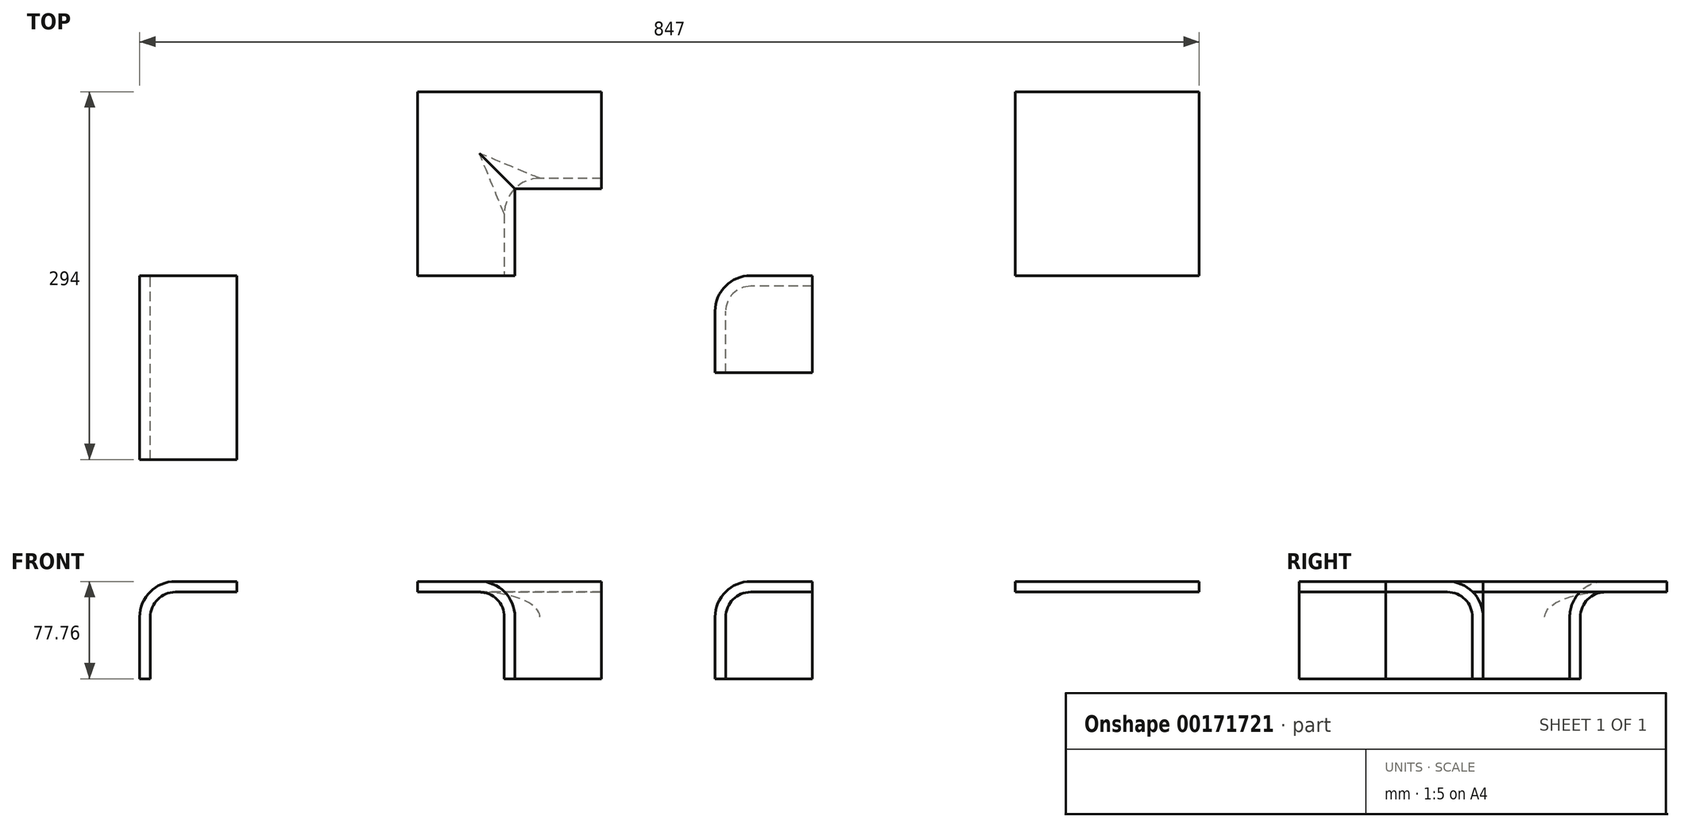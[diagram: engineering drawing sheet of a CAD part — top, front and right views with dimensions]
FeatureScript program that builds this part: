
annotation { "Feature Type Name" : "Feature", "Feature Type Description" : "" }
export const myFeature = defineFeature(function(context is Context, id is Id, definition is map)
    precondition{}
    {
        {
            var Q0;
            Q0=qCreatedBy(makeId("Front.planeOp"),FACE);
            var sketch = newSketch(context, id + "F0", { "sketchPlane" : qUnion([Q0])});
            skLineSegment(sketch, "E0.bottom", {"start": v(-500, 38.88) * mm, "end": v(500, 38.88) * mm, "construction": true});
            skLineSegment(sketch, "E0.top", {"start": v(-500, -38.87) * mm, "end": v(500, -38.87) * mm, "construction": true});
            skLineSegment(sketch, "E0.left", {"start": v(-500, 38.88) * mm, "end": v(-500, -38.87) * mm, "construction": true});
            skLineSegment(sketch, "E0.right", {"start": v(500, 38.87) * mm, "end": v(500, -38.88) * mm, "construction": true});
            skPoint(sketch, "E0.middle", {"position": v(0, 0) * mm});
            skLineSegment(sketch, "E1", {"start": v(-500, -38.87) * mm, "end": v(-500, 38.88) * mm});
            skLineSegment(sketch, "E2", {"start": v(-500, 38.88) * mm, "end": v(-422.25, 38.88) * mm});
            skLineSegment(sketch, "E3", {"start": v(-422.25, 38.88) * mm, "end": v(-422.25, 30.38) * mm});
            skLineSegment(sketch, "E4", {"start": v(-422.25, 30.38) * mm, "end": v(-491.5, 30.38) * mm});
            skLineSegment(sketch, "E5", {"start": v(-491.5, 30.38) * mm, "end": v(-491.5, -38.87) * mm});
            skLineSegment(sketch, "E6", {"start": v(-491.5, -38.87) * mm, "end": v(-500, -38.87) * mm});
            skLineSegment(sketch, "E7", {"start": v(-350, 38.88) * mm, "end": v(-350, -45.08) * mm, "construction": true});
            skLineSegment(sketch, "E8.MirrorCS", {"start": v(-208.5, -38.87) * mm, "end": v(-200, -38.87) * mm});
            skLineSegment(sketch, "E9.MirrorCS", {"start": v(-277.75, 38.88) * mm, "end": v(-277.75, 30.38) * mm});
            skLineSegment(sketch, "E10.MirrorCS", {"start": v(-200, 38.88) * mm, "end": v(-200, -38.87) * mm, "construction": true});
            skLineSegment(sketch, "E11.MirrorCS", {"start": v(-200, 38.88) * mm, "end": v(-1200, 38.88) * mm, "construction": true});
            skLineSegment(sketch, "E12.MirrorCS", {"start": v(-200, -38.87) * mm, "end": v(-1200, -38.87) * mm, "construction": true});
            skLineSegment(sketch, "E13.MirrorCS", {"start": v(-200, -38.87) * mm, "end": v(-200, 38.88) * mm});
            skLineSegment(sketch, "E14.MirrorCS", {"start": v(-277.75, 30.38) * mm, "end": v(-208.5, 30.38) * mm});
            skLineSegment(sketch, "E15.MirrorCS", {"start": v(-208.5, 30.38) * mm, "end": v(-208.5, -38.87) * mm});
            skLineSegment(sketch, "E16.MirrorCS", {"start": v(-200, 38.88) * mm, "end": v(-277.75, 38.88) * mm});
            skLineSegment(sketch, "E17", {"start": v(-120, 38.88) * mm, "end": v(-120, -38.87) * mm, "construction": true});
            skLineSegment(sketch, "E18.MirrorCS", {"start": v(-31.5, -38.87) * mm, "end": v(-40, -38.87) * mm});
            skLineSegment(sketch, "E19.MirrorCS", {"start": v(37.75, 38.88) * mm, "end": v(37.75, 30.38) * mm});
            skLineSegment(sketch, "E20.MirrorCS", {"start": v(-40, 38.88) * mm, "end": v(-40, -38.87) * mm, "construction": true});
            skLineSegment(sketch, "E21.MirrorCS", {"start": v(-40, -38.87) * mm, "end": v(-40, 38.88) * mm});
            skLineSegment(sketch, "E22.MirrorCS", {"start": v(-31.5, 30.38) * mm, "end": v(-31.5, -38.87) * mm});
            skLineSegment(sketch, "E23.MirrorCS", {"start": v(37.75, 30.38) * mm, "end": v(-31.5, 30.38) * mm});
            skLineSegment(sketch, "E24.MirrorCS", {"start": v(-40, 38.88) * mm, "end": v(37.75, 38.88) * mm});
            skPoint(sketch, "E25.oppositeSnap0", {"position": v(500, 0) * mm});
            skLineSegment(sketch, "E25.bottom", {"start": v(200, 38.88) * mm, "end": v(347, 38.88) * mm});
            skLineSegment(sketch, "E25.top", {"start": v(200, 30.38) * mm, "end": v(347, 30.38) * mm});
            skLineSegment(sketch, "E25.left", {"start": v(200, 38.88) * mm, "end": v(200, 30.38) * mm});
            skLineSegment(sketch, "E25.right", {"start": v(347, 38.88) * mm, "end": v(347, 30.38) * mm});
            skSolve(sketch);
        }
        {
            var Q0;
            Q0=makeQuery(id+"F0.imprint","IMPRINT",FACE,{"disambiguationData":[TD([[makeQuery(id+"F0.imprint","IMPRINT",EDGE,{"derivedFrom":sQuery(id+"F0.wireOp",EDGE,"E1")}),-1.0]])]});
            extrude(context, id + "F1", {"entities" : qUnion([Q0]), "depth" : 147 * mm});
        }
        {
            var Q0;
            Q0=makeQuery(id+"F0.imprint","IMPRINT",FACE,{"disambiguationData":[TD([[makeQuery(id+"F0.imprint","IMPRINT",EDGE,{"derivedFrom":sQuery(id+"F0.wireOp",EDGE,"E8.MirrorCS")}),1.0]])]});
            extrude(context, id + "F2", {"entities" : qUnion([Q0]), "oppositeDirection" : true, "depth" : 147 * mm});
        }
        {
            var Q0;
            Q0=makeQuery(id+"F0.imprint","IMPRINT",FACE,{"disambiguationData":[TD([[makeQuery(id+"F0.imprint","IMPRINT",EDGE,{"derivedFrom":sQuery(id+"F0.wireOp",EDGE,"E18.MirrorCS")}),-1.0]])]});
            extrude(context, id + "F3", {"entities" : qUnion([Q0]), "depth" : 77.75 * mm});
        }
        {
            var Q0;
            Q0=makeQuery(id+"F2.opExtrude","SWEPT_FACE",FACE,{"disambiguationData":[OSD([sQuery(id+"F0.wireOp",EDGE,"E13.MirrorCS")])]});
            var sketch = newSketch(context, id + "F4", { "sketchPlane" : qUnion([Q0])});
            skLineSegment(sketch, "E26.0.1", {"start": v(69.25, -38.87) * mm, "end": v(77.75, -38.87) * mm});
            skLineSegment(sketch, "E26.0.2", {"start": v(147, 30.38) * mm, "end": v(147, 38.88) * mm});
            skLineSegment(sketch, "E26.0.3", {"start": v(147, 38.88) * mm, "end": v(69.25, 38.88) * mm});
            skLineSegment(sketch, "E27", {"start": v(69.25, 38.88) * mm, "end": v(69.25, -38.87) * mm});
            skLineSegment(sketch, "E28", {"start": v(77.75, -38.87) * mm, "end": v(77.75, 30.38) * mm});
            skLineSegment(sketch, "E29", {"start": v(77.75, 30.38) * mm, "end": v(147, 30.38) * mm});
            skPoint(sketch, "E30.orphan", {"position": v(147, -38.87) * mm});
            skPoint(sketch, "E26.0.0.end.orphan", {"position": v(0, -38.87) * mm});
            skPoint(sketch, "E26.0.0.start.orphan", {"position": v(0, 38.88) * mm});
            skLineSegment(sketch, "E31", {"start": v(77.75, -38.87) * mm, "end": v(69.25, -38.87) * mm});
            skSolve(sketch);
        }
        {
            var Q0;
            Q0=makeQuery(id+"F4.imprint","IMPRINT",FACE,{"disambiguationData":[TD([[makeQuery(id+"F4.imprint","IMPRINT",EDGE,{"derivedFrom":sQuery(id+"F4.wireOp",EDGE,"E26.0.3")}),1.0]])]});
            extrude(context, id + "F5", {"entities" : qUnion([Q0]), "operationType" : NewBodyOperationType.ADD, "depth" : 69.25 * mm});
        }
        {
            var Q0;
            {var subQ0=sQuery(id+"F0.wireOp",EDGE,"E13.MirrorCS");Q0=makeQuery(id+"F5.boolean.opBoolean","SPLIT",FACE,{"disambiguationData":[TD([makeQuery(id+"F5.opExtrude","SWEPT_FACE",FACE,{"disambiguationData":[OSD([sQuery(id+"F4.wireOp",EDGE,"E28")])]})])],"derivedFrom":makeQuery(id+"F2.opExtrude","SWEPT_FACE",FACE,{"disambiguationData":[OSD([subQ0])]})});}
            extrude(context, id + "F6", {"entities" : qUnion([Q0]), "operationType" : NewBodyOperationType.REMOVE, "oppositeDirection" : true, "depth" : 25 * mm});
        }
        {
            var Q0;
            Q0=makeQuery(id+"F0.imprint","IMPRINT",FACE,{"disambiguationData":[TD([[makeQuery(id+"F0.imprint","IMPRINT",EDGE,{"derivedFrom":sQuery(id+"F0.wireOp",EDGE,"E18.MirrorCS")}),-1.0]])]});
            var sketch = newSketch(context, id + "F7", { "sketchPlane" : qUnion([Q0])});
            skLineSegment(sketch, "E32.0", {"start": v(-40, 38.88) * mm, "end": v(37.75, 38.88) * mm});
            skLineSegment(sketch, "E33.0", {"start": v(-40, -38.87) * mm, "end": v(-40, 38.88) * mm});
            skLineSegment(sketch, "E34", {"start": v(37.75, 38.88) * mm, "end": v(37.75, -38.87) * mm});
            skLineSegment(sketch, "E35", {"start": v(37.75, -38.87) * mm, "end": v(-40, -38.87) * mm});
            skSolve(sketch);
        }
        {
            var Q0;
            Q0 = qSketchRegion(id + "F7", true);
            extrude(context, id + "F8", {"entities" : qUnion([Q0]), "operationType" : NewBodyOperationType.ADD, "depth" : 8.5 * mm});
        }
        {
            var Q0;
            Q0=makeQuery(id+"F3.opExtrude","SWEPT_EDGE",EDGE,{"disambiguationData":[OSD([sQuery(id+"F0.wireOp",EDGE,"E22.MirrorCS"),sQuery(id+"F0.wireOp",EDGE,"E23.MirrorCS")])]});
            var Q1;
            Q1=makeQuery(id+"F8.boolean.opBoolean","INTERSECT",EDGE,{"derivedFrom":[makeQuery(id+"F3.opExtrude","SWEPT_FACE",FACE,{"disambiguationData":[OSD([sQuery(id+"F0.wireOp",EDGE,"E23.MirrorCS")])]}),makeQuery(id+"F8.opExtrude","CAP_FACE",FACE,{"disambiguationData":[OSD([sQuery(id+"F7.wireOp",EDGE,"E32.0"),sQuery(id+"F7.wireOp",EDGE,"E33.0"),sQuery(id+"F7.wireOp",EDGE,"E34"),sQuery(id+"F7.wireOp",EDGE,"E35")])],"isStart":false})]});
            var Q2;
            Q2=makeQuery(id+"F8.boolean.opBoolean","INTERSECT",EDGE,{"derivedFrom":[makeQuery(id+"F3.opExtrude","SWEPT_FACE",FACE,{"disambiguationData":[OSD([sQuery(id+"F0.wireOp",EDGE,"E22.MirrorCS")])]}),makeQuery(id+"F8.opExtrude","CAP_FACE",FACE,{"disambiguationData":[OSD([sQuery(id+"F7.wireOp",EDGE,"E32.0"),sQuery(id+"F7.wireOp",EDGE,"E33.0"),sQuery(id+"F7.wireOp",EDGE,"E34"),sQuery(id+"F7.wireOp",EDGE,"E35")])],"isStart":false})]});
            var Q3;
            Q3=makeQuery(id+"F5.opExtrude","CAP_EDGE",EDGE,{"disambiguationData":[OSD([sQuery(id+"F4.wireOp",EDGE,"E27")])],"isStart":true});
            var Q4;
            {var subQ0=sQuery(id+"F4.wireOp",EDGE,"E29");var subQ1=sQuery(id+"F4.wireOp",EDGE,"E28");Q4=makeQuery(id+"F6.boolean.opBoolean","MERGE",EDGE,{"derivedFrom":[makeQuery(id+"F5.opExtrude","SWEPT_EDGE",EDGE,{"disambiguationData":[OSD([subQ1,subQ0])]}),makeQuery(id+"F6.opExtrude","SWEPT_EDGE",EDGE,{"disambiguationData":[OSD([subQ1,subQ0])]})]});}
            var Q5;
            Q5=makeQuery(id+"F2.opExtrude","SWEPT_EDGE",EDGE,{"disambiguationData":[OSD([sQuery(id+"F0.wireOp",EDGE,"E14.MirrorCS"),sQuery(id+"F0.wireOp",EDGE,"E15.MirrorCS")])]});
            var Q6;
            Q6=makeQuery(id+"F1.opExtrude","SWEPT_EDGE",EDGE,{"disambiguationData":[OSD([sQuery(id+"F0.wireOp",EDGE,"E4"),sQuery(id+"F0.wireOp",EDGE,"E5")])]});
            fillet(context, id + "F9", {"entities" : qUnion([Q0, Q1, Q2, Q3, Q4, Q5, Q6]), "radius" : 20 * mm, "tangentPropagation" : true, "allowEdgeOverflow" : false});
        }
        {
            var Q0;
            Q0=makeQuery(id+"F1.opExtrude","SWEPT_EDGE",EDGE,{"disambiguationData":[OSD([sQuery(id+"F0.wireOp",EDGE,"E1"),sQuery(id+"F0.wireOp",EDGE,"E2")])]});
            var Q1;
            Q1=makeQuery(id+"F2.opExtrude","SWEPT_EDGE",EDGE,{"disambiguationData":[OSD([sQuery(id+"F0.wireOp",EDGE,"E13.MirrorCS"),sQuery(id+"F0.wireOp",EDGE,"E16.MirrorCS")])]});
            var Q2;
            Q2=makeQuery(id+"F9.opFillet","BLEND_EDGE",EDGE,{"blendedFrom":[makeQuery(id+"F5.opExtrude","CAP_EDGE",EDGE,{"disambiguationData":[OSD([sQuery(id+"F4.wireOp",EDGE,"E27")])],"isStart":true}),makeQuery(id+"F5.boolean.opBoolean","MERGE",FACE,{"derivedFrom":[makeQuery(id+"F2.opExtrude","SWEPT_FACE",FACE,{"disambiguationData":[OSD([sQuery(id+"F0.wireOp",EDGE,"E16.MirrorCS")])]}),makeQuery(id+"F5.opExtrude","SWEPT_FACE",FACE,{"disambiguationData":[OSD([sQuery(id+"F4.wireOp",EDGE,"E26.0.3")])]})]})],"blendedInto":[makeQuery(id+"F5.boolean.opBoolean","MERGE",FACE,{"derivedFrom":[makeQuery(id+"F2.opExtrude","SWEPT_FACE",FACE,{"disambiguationData":[OSD([sQuery(id+"F0.wireOp",EDGE,"E16.MirrorCS")])]}),makeQuery(id+"F5.opExtrude","SWEPT_FACE",FACE,{"disambiguationData":[OSD([sQuery(id+"F4.wireOp",EDGE,"E26.0.3")])]})]})]});
            var Q3;
            Q3=makeQuery(id+"F5.opExtrude","SWEPT_EDGE",EDGE,{"disambiguationData":[OSD([sQuery(id+"F0.wireOp",EDGE,"E13.MirrorCS"),sQuery(id+"F0.wireOp",EDGE,"E16.MirrorCS"),sQuery(id+"F4.wireOp",EDGE,"E26.0.3"),sQuery(id+"F4.wireOp",EDGE,"E27")])]});
            var Q4;
            Q4=makeQuery(id+"F6.boolean.opBoolean","INTERSECT",EDGE,{"derivedFrom":[makeQuery(id+"F2.opExtrude","SWEPT_FACE",FACE,{"disambiguationData":[OSD([sQuery(id+"F0.wireOp",EDGE,"E15.MirrorCS")])]}),makeQuery(id+"F6.opExtrude","SWEPT_FACE",FACE,{"disambiguationData":[OSD([sQuery(id+"F4.wireOp",EDGE,"E28")])]})]});
            var Q5;
            {var subQ0=sQuery(id+"F4.wireOp",EDGE,"E29");var subQ1=sQuery(id+"F4.wireOp",EDGE,"E28");Q5=makeQuery(id+"F9.opFillet","BLEND_EDGE",EDGE,{"blendedFrom":[makeQuery(id+"F6.boolean.opBoolean","MERGE",EDGE,{"derivedFrom":[makeQuery(id+"F5.opExtrude","SWEPT_EDGE",EDGE,{"disambiguationData":[OSD([subQ1,subQ0])]}),makeQuery(id+"F6.opExtrude","SWEPT_EDGE",EDGE,{"disambiguationData":[OSD([subQ1,subQ0])]})]}),makeQuery(id+"F2.opExtrude","SWEPT_EDGE",EDGE,{"disambiguationData":[OSD([sQuery(id+"F0.wireOp",EDGE,"E14.MirrorCS"),sQuery(id+"F0.wireOp",EDGE,"E15.MirrorCS")])]})],"blendedInto":[]});}
            var Q6;
            Q6=makeQuery(id+"F3.opExtrude","SWEPT_EDGE",EDGE,{"disambiguationData":[OSD([sQuery(id+"F0.wireOp",EDGE,"E21.MirrorCS"),sQuery(id+"F0.wireOp",EDGE,"E24.MirrorCS")])]});
            var Q7;
            Q7=makeQuery(id+"F3.opExtrude","CAP_EDGE",EDGE,{"disambiguationData":[OSD([sQuery(id+"F0.wireOp",EDGE,"E21.MirrorCS")])],"isStart":true});
            var Q8;
            Q8=makeQuery(id+"F3.opExtrude","CAP_EDGE",EDGE,{"disambiguationData":[OSD([sQuery(id+"F0.wireOp",EDGE,"E24.MirrorCS")])],"isStart":true});
            fillet(context, id + "F10", {"entities" : qUnion([Q0, Q1, Q2, Q3, Q4, Q5, Q6, Q7, Q8]), "radius" : 28.5 * mm, "tangentPropagation" : true, "allowEdgeOverflow" : false});
        }
        {
            var Q0;
            Q0=makeQuery(id+"F0.imprint","IMPRINT",FACE,{"disambiguationData":[TD([[makeQuery(id+"F0.imprint","IMPRINT",EDGE,{"derivedFrom":sQuery(id+"F0.wireOp",EDGE,"E25.bottom")}),-1.0]])]});
            extrude(context, id + "F11", {"entities" : qUnion([Q0]), "oppositeDirection" : true, "depth" : 147 * mm});
        }
    });
